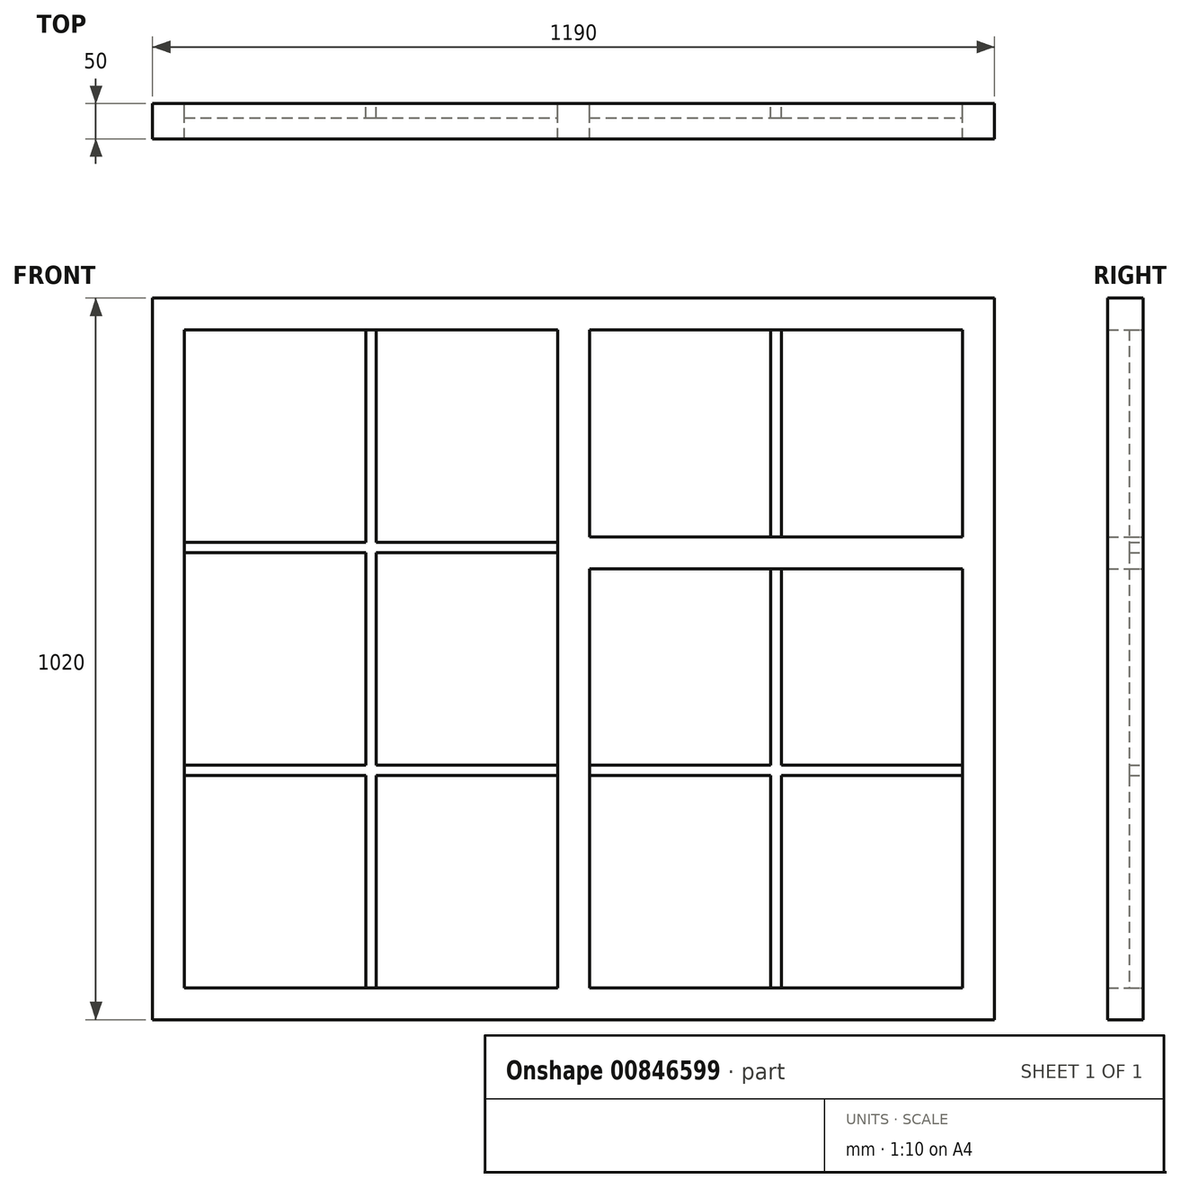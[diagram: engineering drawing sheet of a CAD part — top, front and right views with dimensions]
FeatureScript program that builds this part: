
annotation { "Feature Type Name" : "Feature", "Feature Type Description" : "" }
export const myFeature = defineFeature(function(context is Context, id is Id, definition is map)
    precondition{}
    {
        {
            var Q0;
            Q0=qCreatedBy(makeId("Front.planeOp"),FACE);
            var sketch = newSketch(context, id + "F0", { "sketchPlane" : qUnion([Q0])});
            skLineSegment(sketch, "E0.bottom", {"start": v(0, 0) * mm, "end": v(1190, 0) * mm});
            skLineSegment(sketch, "E0.top", {"start": v(0, 1020) * mm, "end": v(1190, 1020) * mm});
            skLineSegment(sketch, "E0.left", {"start": v(0, 0) * mm, "end": v(0, 1020) * mm});
            skLineSegment(sketch, "E0.right", {"start": v(1190, 0) * mm, "end": v(1190, 1020) * mm});
            skLineSegment(sketch, "E1.bottom", {"start": v(45, 975) * mm, "end": v(572.5, 975) * mm});
            skLineSegment(sketch, "E1.top", {"start": v(45, 45) * mm, "end": v(572.5, 45) * mm});
            skLineSegment(sketch, "E1.left", {"start": v(45, 975) * mm, "end": v(45, 45) * mm});
            skLineSegment(sketch, "E1.right", {"start": v(572.5, 975) * mm, "end": v(572.5, 45) * mm});
            skLineSegment(sketch, "E2.bottom", {"start": v(617.5, 975) * mm, "end": v(1145, 975) * mm});
            skLineSegment(sketch, "E2.top", {"start": v(617.5, 682.5) * mm, "end": v(1145, 682.5) * mm});
            skLineSegment(sketch, "E2.left", {"start": v(617.5, 975) * mm, "end": v(617.5, 682.5) * mm});
            skLineSegment(sketch, "E2.right", {"start": v(1145, 975) * mm, "end": v(1145, 682.5) * mm});
            skLineSegment(sketch, "E3.bottom", {"start": v(617.5, 637.5) * mm, "end": v(1145, 637.5) * mm});
            skLineSegment(sketch, "E3.top", {"start": v(617.5, 45) * mm, "end": v(1145, 45) * mm});
            skLineSegment(sketch, "E3.left", {"start": v(617.5, 637.5) * mm, "end": v(617.5, 45) * mm});
            skLineSegment(sketch, "E3.right", {"start": v(1145, 637.5) * mm, "end": v(1145, 45) * mm});
            skSolve(sketch);
        }
        {
            var Q0;
            Q0=qSketchRegion(id+"F0",true);
            extrude(context, id + "F1", {"entities" : qUnion([Q0]), "depth" : 50 * mm, "offsetDistance" : 25 * mm});
        }
        {
            var Q0;
            Q0=qCreatedBy(makeId("Front.planeOp"),FACE);
            var sketch = newSketch(context, id + "F2", { "sketchPlane" : qUnion([Q0])});
            skLineSegment(sketch, "E4.bottom", {"start": v(301.25, 975) * mm, "end": v(316.25, 975) * mm});
            skLineSegment(sketch, "E4.top", {"start": v(301.25, 45) * mm, "end": v(316.25, 45) * mm});
            skLineSegment(sketch, "E4.left", {"start": v(301.25, 975) * mm, "end": v(301.25, 675) * mm});
            skLineSegment(sketch, "E4.right", {"start": v(316.25, 975) * mm, "end": v(316.25, 675) * mm});
            skLineSegment(sketch, "E5.bottom", {"start": v(45, 675) * mm, "end": v(301.25, 675) * mm});
            skLineSegment(sketch, "E5.top", {"start": v(45, 660) * mm, "end": v(301.25, 660) * mm});
            skLineSegment(sketch, "E5.left", {"start": v(45, 675) * mm, "end": v(45, 660) * mm});
            skLineSegment(sketch, "E5.right", {"start": v(572.5, 675) * mm, "end": v(572.5, 660) * mm});
            skLineSegment(sketch, "E6.bottom", {"start": v(45, 360) * mm, "end": v(301.25, 360) * mm});
            skLineSegment(sketch, "E6.top", {"start": v(45, 345) * mm, "end": v(301.25, 345) * mm});
            skLineSegment(sketch, "E6.left", {"start": v(45, 360) * mm, "end": v(45, 345) * mm});
            skLineSegment(sketch, "E6.right", {"start": v(572.5, 360) * mm, "end": v(572.5, 345) * mm});
            skLineSegment(sketch, "E7.trimOffspring", {"start": v(316.25, 675) * mm, "end": v(572.5, 675) * mm});
            skLineSegment(sketch, "E8.trimOffspring", {"start": v(301.25, 660) * mm, "end": v(301.25, 360) * mm});
            skLineSegment(sketch, "E9.trimOffspring", {"start": v(316.25, 660) * mm, "end": v(572.5, 660) * mm});
            skLineSegment(sketch, "E10.trimOffspring", {"start": v(316.25, 660) * mm, "end": v(316.25, 360) * mm});
            skLineSegment(sketch, "E11.trimOffspring", {"start": v(316.25, 360) * mm, "end": v(572.5, 360) * mm});
            skLineSegment(sketch, "E12.trimOffspring", {"start": v(301.25, 345) * mm, "end": v(301.25, 45) * mm});
            skLineSegment(sketch, "E13.trimOffspring", {"start": v(316.25, 345) * mm, "end": v(572.5, 345) * mm});
            skLineSegment(sketch, "E14.trimOffspring", {"start": v(316.25, 345) * mm, "end": v(316.25, 45) * mm});
            skLineSegment(sketch, "E15.bottom", {"start": v(617.5, 360) * mm, "end": v(873.75, 360) * mm});
            skLineSegment(sketch, "E15.top", {"start": v(617.5, 345) * mm, "end": v(873.75, 345) * mm});
            skLineSegment(sketch, "E15.left", {"start": v(617.5, 360) * mm, "end": v(617.5, 345) * mm});
            skLineSegment(sketch, "E15.right", {"start": v(1145, 360) * mm, "end": v(1145, 345) * mm});
            skLineSegment(sketch, "E16.bottom", {"start": v(873.75, 637.5) * mm, "end": v(888.75, 637.5) * mm});
            skLineSegment(sketch, "E16.top", {"start": v(873.75, 45) * mm, "end": v(888.75, 45) * mm});
            skLineSegment(sketch, "E16.left", {"start": v(873.75, 637.5) * mm, "end": v(873.75, 360) * mm});
            skLineSegment(sketch, "E16.right", {"start": v(888.75, 637.5) * mm, "end": v(888.75, 360) * mm});
            skLineSegment(sketch, "E17.bottom", {"start": v(873.75, 975) * mm, "end": v(888.75, 975) * mm});
            skLineSegment(sketch, "E17.top", {"start": v(873.75, 682.5) * mm, "end": v(888.75, 682.5) * mm});
            skLineSegment(sketch, "E17.left", {"start": v(873.75, 975) * mm, "end": v(873.75, 682.5) * mm});
            skLineSegment(sketch, "E17.right", {"start": v(888.75, 975) * mm, "end": v(888.75, 682.5) * mm});
            skLineSegment(sketch, "E18.trimOffspring", {"start": v(888.75, 360) * mm, "end": v(1145, 360) * mm});
            skLineSegment(sketch, "E19.trimOffspring", {"start": v(873.75, 345) * mm, "end": v(873.75, 45) * mm});
            skLineSegment(sketch, "E20.trimOffspring", {"start": v(888.75, 345) * mm, "end": v(1145, 345) * mm});
            skLineSegment(sketch, "E21.trimOffspring", {"start": v(888.75, 345) * mm, "end": v(888.75, 45) * mm});
            skSolve(sketch);
        }
        {
            var Q0;
            Q0 = qSketchRegion(id + "F2", true);
            extrude(context, id + "F3", {"entities" : qUnion([Q0]), "operationType" : NewBodyOperationType.ADD, "depth" : 20 * mm, "offsetDistance" : 25 * mm});
        }
    });
